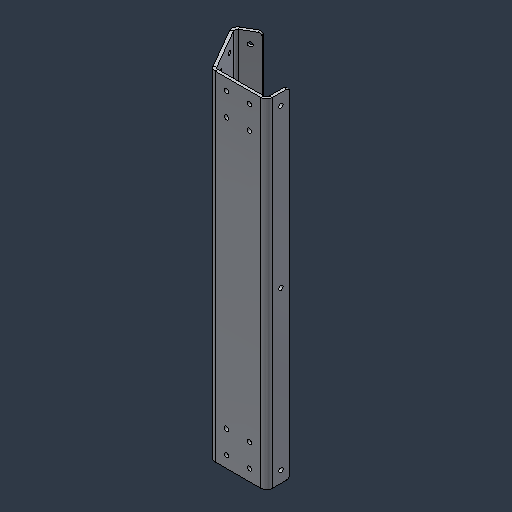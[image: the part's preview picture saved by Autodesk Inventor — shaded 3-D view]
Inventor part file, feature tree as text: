
AUTODESK INVENTOR PART (.ipt)
format: ipt  version: 2024.3 (Build 283343000, 343)  size: 121,344 bytes
history: native  units: mm (DEFAULTED — no unit token found)
features: fillet x1
ambient origin geometry x8: Origin, YZ Plane, XZ Plane, XY Plane, X Axis, Y Axis, Z Axis, Center Point
bodies: Solid1 (feature_tree)
feature tree (1):
  fillet  "Fillet1"  [1 undecoded]
note: 1 required parameter value undecoded (feature->parameter linkage not recoverable at this tier; creation-order binding heuristic only, values carry confidence <= 0.55)
